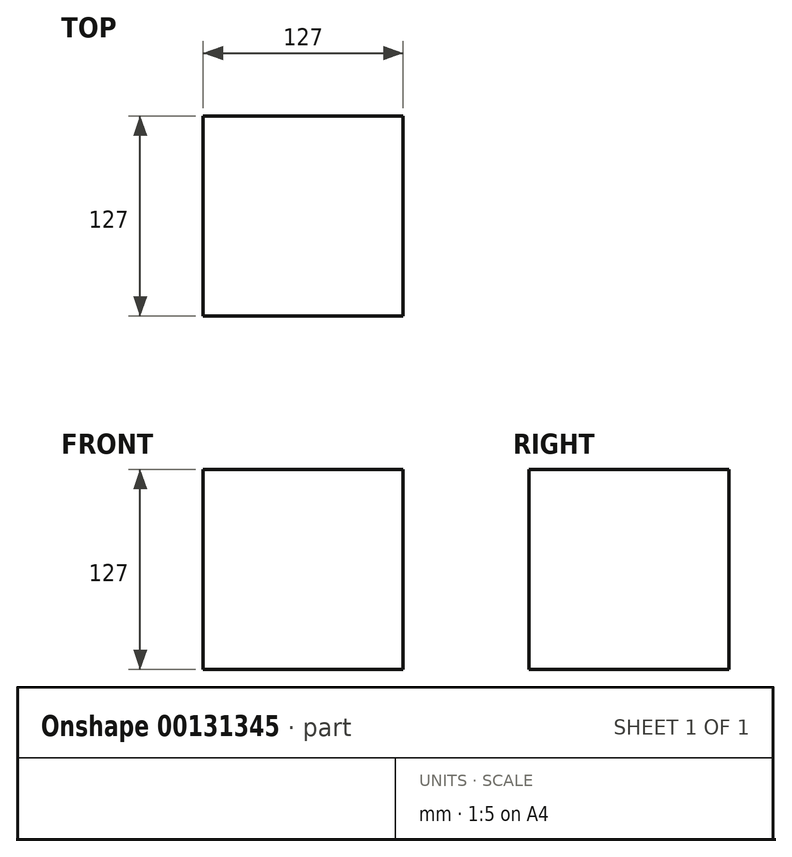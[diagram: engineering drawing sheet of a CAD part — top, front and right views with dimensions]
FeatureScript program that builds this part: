
annotation { "Feature Type Name" : "Feature", "Feature Type Description" : "" }
export const myFeature = defineFeature(function(context is Context, id is Id, definition is map)
    precondition{}
    {
        {
            var Q0;
            Q0=qCreatedBy(makeId("Right.planeOp"),FACE);
            var sketch = newSketch(context, id + "F0", { "sketchPlane" : qUnion([Q0])});
            skLineSegment(sketch, "E0.bottom", {"start": v(-63.5, -63.5) * mm, "end": v(63.5, -63.5) * mm});
            skLineSegment(sketch, "E0.top", {"start": v(-63.5, 63.5) * mm, "end": v(63.5, 63.5) * mm});
            skLineSegment(sketch, "E0.left", {"start": v(-63.5, -63.5) * mm, "end": v(-63.5, 63.5) * mm});
            skLineSegment(sketch, "E0.right", {"start": v(63.5, -63.5) * mm, "end": v(63.5, 63.5) * mm});
            skPoint(sketch, "E0.middle", {"position": v(0, 0) * mm});
            skSolve(sketch);
        }
        {
            var Q0;
            Q0 = qSketchRegion(id + "F0", true);
            extrude(context, id + "F1", {"entities" : qUnion([Q0]), "endBound" : BoundingType.SYMMETRIC, "depth" : 127 * mm});
        }
    });
